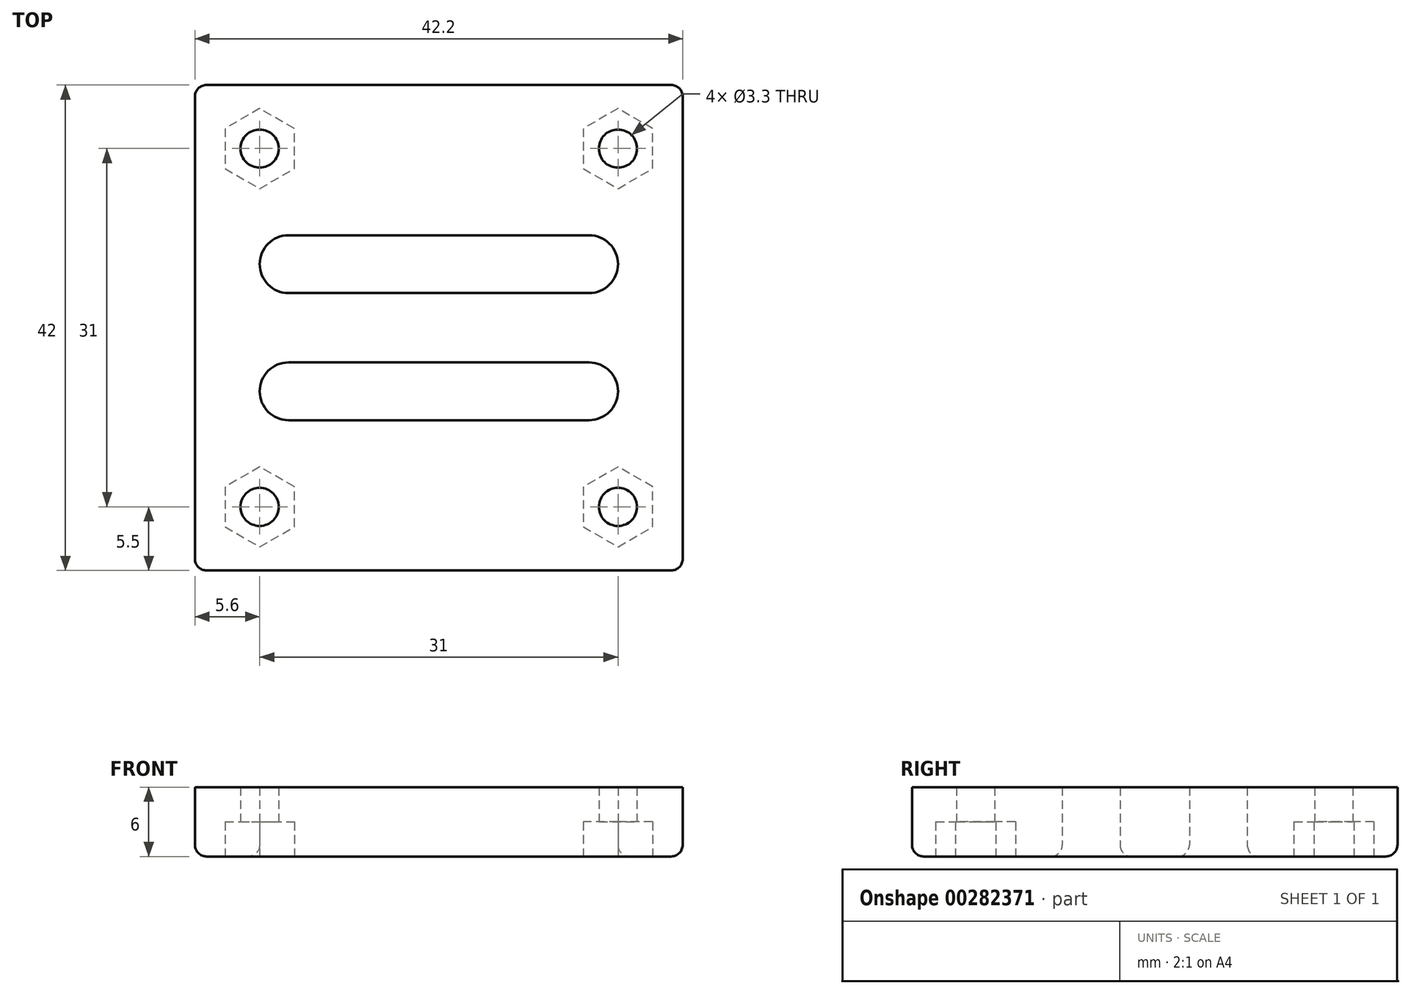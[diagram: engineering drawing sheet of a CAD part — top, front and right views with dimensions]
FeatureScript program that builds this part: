
annotation { "Feature Type Name" : "Feature", "Feature Type Description" : "" }
export const myFeature = defineFeature(function(context is Context, id is Id, definition is map)
    precondition{}
    {
        {
            var Q0;
            Q0=qCreatedBy(makeId("Top.planeOp"),FACE);
            var sketch = newSketch(context, id + "F0", { "sketchPlane" : qUnion([Q0])});
            skLineSegment(sketch, "E0.bottom", {"start": v(21.1, 21) * mm, "end": v(-21.1, 21) * mm});
            skLineSegment(sketch, "E0.top", {"start": v(21.1, -21) * mm, "end": v(-21.1, -21) * mm});
            skLineSegment(sketch, "E0.left", {"start": v(21.1, 21) * mm, "end": v(21.1, -21) * mm});
            skLineSegment(sketch, "E0.right", {"start": v(-21.1, 21) * mm, "end": v(-21.1, -21) * mm});
            skPoint(sketch, "E0.middle", {"position": v(0, 0) * mm});
            skLineSegment(sketch, "E1.bottom", {"start": v(15.5, 15.5) * mm, "end": v(-15.5, 15.5) * mm, "construction": true});
            skLineSegment(sketch, "E1.top", {"start": v(15.5, -15.5) * mm, "end": v(-15.5, -15.5) * mm, "construction": true});
            skLineSegment(sketch, "E1.left", {"start": v(15.5, 15.5) * mm, "end": v(15.5, -15.5) * mm, "construction": true});
            skLineSegment(sketch, "E1.right", {"start": v(-15.5, 15.5) * mm, "end": v(-15.5, -15.5) * mm, "construction": true});
            skLineSegment(sketch, "E2", {"start": v(0, -15.5) * mm, "end": v(0, 15.5) * mm, "construction": true});
            skLineSegment(sketch, "E3", {"start": v(-13, 5.5) * mm, "end": v(13, 5.5) * mm, "construction": true});
            skLineSegment(sketch, "E4", {"start": v(-13, -5.5) * mm, "end": v(13, -5.5) * mm, "construction": true});
            skArc(sketch, "E5.0.startCap", {"start": v(-13, -8) * mm, "mid": v(-15.5, -5.5) * mm, "end": v(-13, -3) * mm});
            skArc(sketch, "E5.0.endCap", {"start": v(13, -3) * mm, "mid": v(15.5, -5.5) * mm, "end": v(13, -8) * mm});
            skLineSegment(sketch, "E5.0.left", {"start": v(-13, -3) * mm, "end": v(13, -3) * mm});
            skLineSegment(sketch, "E5.0.right", {"start": v(-13, -8) * mm, "end": v(13, -8) * mm});
            skArc(sketch, "E6.0.startCap", {"start": v(-13, 3) * mm, "mid": v(-15.5, 5.5) * mm, "end": v(-13, 8) * mm});
            skArc(sketch, "E6.0.endCap", {"start": v(13, 8) * mm, "mid": v(15.5, 5.5) * mm, "end": v(13, 3) * mm});
            skLineSegment(sketch, "E6.0.left", {"start": v(-13, 8) * mm, "end": v(13, 8) * mm});
            skLineSegment(sketch, "E6.0.right", {"start": v(-13, 3) * mm, "end": v(13, 3) * mm});
            skSolve(sketch);
        }
        {
            var Q0;
            Q0=qSketchRegion(id+"F0",true);
            extrude(context, id + "F1", {"entities" : qUnion([Q0]), "depth" : 6 * mm});
        }
        {
            var Q0;
            Q0=makeQuery(id+"F1.opExtrude","CAP_FACE",FACE,{"disambiguationData":[OSD([sQuery(id+"F0.wireOp",EDGE,"E0.bottom"),sQuery(id+"F0.wireOp",EDGE,"E0.top"),sQuery(id+"F0.wireOp",EDGE,"E0.left"),sQuery(id+"F0.wireOp",EDGE,"E0.right"),sQuery(id+"F0.wireOp",EDGE,"E5.0.startCap"),sQuery(id+"F0.wireOp",EDGE,"E5.0.endCap"),sQuery(id+"F0.wireOp",EDGE,"E5.0.left"),sQuery(id+"F0.wireOp",EDGE,"E5.0.right"),sQuery(id+"F0.wireOp",EDGE,"E6.0.startCap"),sQuery(id+"F0.wireOp",EDGE,"E6.0.endCap"),sQuery(id+"F0.wireOp",EDGE,"E6.0.left"),sQuery(id+"F0.wireOp",EDGE,"E6.0.right")])],"isStart":true});
            var sketch = newSketch(context, id + "F2", { "sketchPlane" : qUnion([Q0])});
            skLineSegment(sketch, "E7.bottom", {"start": v(15.5, 15.5) * mm, "end": v(-15.5, 15.5) * mm, "construction": true});
            skLineSegment(sketch, "E7.top", {"start": v(15.5, -15.5) * mm, "end": v(-15.5, -15.5) * mm, "construction": true});
            skLineSegment(sketch, "E7.left", {"start": v(15.5, 15.5) * mm, "end": v(15.5, -15.5) * mm, "construction": true});
            skLineSegment(sketch, "E7.right", {"start": v(-15.5, 15.5) * mm, "end": v(-15.5, -15.5) * mm, "construction": true});
            skPoint(sketch, "E7.middle", {"position": v(0, 0) * mm});
            skPoint(sketch, "E8", {"position": v(-15.5, 15.5) * mm});
            skPoint(sketch, "E9", {"position": v(15.5, 15.5) * mm});
            skPoint(sketch, "E10", {"position": v(15.5, -15.5) * mm});
            skPoint(sketch, "E11", {"position": v(-15.5, -15.5) * mm});
            skCircle(sketch, "E12.cCircle", {"center": v(-15.5, 15.5) * mm, "radius": 3 * mm, "construction": true});
            skLineSegment(sketch, "E12.0", {"start": v(-12.5, 17.23) * mm, "end": v(-12.5, 13.77) * mm});
            skLineSegment(sketch, "E12.1", {"start": v(-12.5, 13.77) * mm, "end": v(-15.5, 12.04) * mm});
            skLineSegment(sketch, "E12.2", {"start": v(-15.5, 12.04) * mm, "end": v(-18.5, 13.77) * mm});
            skLineSegment(sketch, "E12.3", {"start": v(-18.5, 13.77) * mm, "end": v(-18.5, 17.23) * mm});
            skLineSegment(sketch, "E12.4", {"start": v(-18.5, 17.23) * mm, "end": v(-15.5, 18.96) * mm});
            skLineSegment(sketch, "E12.5", {"start": v(-15.5, 18.96) * mm, "end": v(-12.5, 17.23) * mm});
            skPoint(sketch, "E12.0.midPoint", {"position": v(-12.5, 15.5) * mm});
            skCircle(sketch, "E13.cCircle", {"center": v(15.5, 15.5) * mm, "radius": 3 * mm, "construction": true});
            skLineSegment(sketch, "E13.0", {"start": v(12.5, 13.77) * mm, "end": v(12.5, 17.23) * mm});
            skLineSegment(sketch, "E13.1", {"start": v(12.5, 17.23) * mm, "end": v(15.5, 18.96) * mm});
            skLineSegment(sketch, "E13.2", {"start": v(15.5, 18.96) * mm, "end": v(18.5, 17.23) * mm});
            skLineSegment(sketch, "E13.3", {"start": v(18.5, 17.23) * mm, "end": v(18.5, 13.77) * mm});
            skLineSegment(sketch, "E13.4", {"start": v(18.5, 13.77) * mm, "end": v(15.5, 12.04) * mm});
            skLineSegment(sketch, "E13.5", {"start": v(15.5, 12.04) * mm, "end": v(12.5, 13.77) * mm});
            skPoint(sketch, "E13.0.midPoint", {"position": v(12.5, 15.5) * mm});
            skCircle(sketch, "E14.cCircle", {"center": v(15.5, -15.5) * mm, "radius": 3 * mm, "construction": true});
            skLineSegment(sketch, "E14.0", {"start": v(12.5, -17.23) * mm, "end": v(12.5, -13.77) * mm});
            skLineSegment(sketch, "E14.1", {"start": v(12.5, -13.77) * mm, "end": v(15.5, -12.04) * mm});
            skLineSegment(sketch, "E14.2", {"start": v(15.5, -12.04) * mm, "end": v(18.5, -13.77) * mm});
            skLineSegment(sketch, "E14.3", {"start": v(18.5, -13.77) * mm, "end": v(18.5, -17.23) * mm});
            skLineSegment(sketch, "E14.4", {"start": v(18.5, -17.23) * mm, "end": v(15.5, -18.96) * mm});
            skLineSegment(sketch, "E14.5", {"start": v(15.5, -18.96) * mm, "end": v(12.5, -17.23) * mm});
            skPoint(sketch, "E14.0.midPoint", {"position": v(12.5, -15.5) * mm});
            skCircle(sketch, "E15.cCircle", {"center": v(-15.5, -15.5) * mm, "radius": 3 * mm, "construction": true});
            skLineSegment(sketch, "E15.0", {"start": v(-12.5, -13.77) * mm, "end": v(-12.5, -17.23) * mm});
            skLineSegment(sketch, "E15.1", {"start": v(-12.5, -17.23) * mm, "end": v(-15.5, -18.96) * mm});
            skLineSegment(sketch, "E15.2", {"start": v(-15.5, -18.96) * mm, "end": v(-18.5, -17.23) * mm});
            skLineSegment(sketch, "E15.3", {"start": v(-18.5, -17.23) * mm, "end": v(-18.5, -13.77) * mm});
            skLineSegment(sketch, "E15.4", {"start": v(-18.5, -13.77) * mm, "end": v(-15.5, -12.04) * mm});
            skLineSegment(sketch, "E15.5", {"start": v(-15.5, -12.04) * mm, "end": v(-12.5, -13.77) * mm});
            skPoint(sketch, "E15.0.midPoint", {"position": v(-12.5, -15.5) * mm});
            skSolve(sketch);
        }
        {
            var Q0;
            Q0=makeQuery(id+"F1.opExtrude","SWEPT_EDGE",EDGE,{"disambiguationData":[OSD([sQuery(id+"F0.wireOp",EDGE,"E0.top"),sQuery(id+"F0.wireOp",EDGE,"E0.right")])]});
            var Q1;
            Q1=makeQuery(id+"F1.opExtrude","SWEPT_EDGE",EDGE,{"disambiguationData":[OSD([sQuery(id+"F0.wireOp",EDGE,"E0.top"),sQuery(id+"F0.wireOp",EDGE,"E0.left")])]});
            var Q2;
            Q2=makeQuery(id+"F1.opExtrude","SWEPT_EDGE",EDGE,{"disambiguationData":[OSD([sQuery(id+"F0.wireOp",EDGE,"E0.bottom"),sQuery(id+"F0.wireOp",EDGE,"E0.right")])]});
            var Q3;
            Q3=makeQuery(id+"F1.opExtrude","SWEPT_EDGE",EDGE,{"disambiguationData":[OSD([sQuery(id+"F0.wireOp",EDGE,"E0.bottom"),sQuery(id+"F0.wireOp",EDGE,"E0.left")])]});
            fillet(context, id + "F3", {"entities" : qUnion([Q0, Q1, Q2, Q3]), "radius" : 1 * mm, "tangentPropagation" : true, "allowEdgeOverflow" : false});
        }
        {
            var Q0;
            Q0=makeQuery(id+"F1.opExtrude","CAP_EDGE",EDGE,{"disambiguationData":[OSD([sQuery(id+"F0.wireOp",EDGE,"E0.top")])],"isStart":true});
            var Q1;
            Q1=makeQuery(id+"F1.opExtrude","CAP_EDGE",EDGE,{"disambiguationData":[OSD([sQuery(id+"F0.wireOp",EDGE,"E5.0.left")])],"isStart":true});
            var Q2;
            Q2=makeQuery(id+"F1.opExtrude","CAP_EDGE",EDGE,{"disambiguationData":[OSD([sQuery(id+"F0.wireOp",EDGE,"E6.0.left")])],"isStart":true});
            fillet(context, id + "F4", {"entities" : qUnion([Q0, Q1, Q2]), "radius" : 1 * mm, "tangentPropagation" : true, "allowEdgeOverflow" : false});
        }
        {
            var Q0;
            Q0 = qSketchRegion(id + "F2", true);
            extrude(context, id + "F5", {"entities" : qUnion([Q0]), "operationType" : NewBodyOperationType.REMOVE, "oppositeDirection" : true, "depth" : 3 * mm});
        }
        {
            var Q0;
            Q0=makeQuery(id+"F1.opExtrude","CAP_FACE",FACE,{"disambiguationData":[OSD([sQuery(id+"F0.wireOp",EDGE,"E0.bottom"),sQuery(id+"F0.wireOp",EDGE,"E0.top"),sQuery(id+"F0.wireOp",EDGE,"E0.left"),sQuery(id+"F0.wireOp",EDGE,"E0.right"),sQuery(id+"F0.wireOp",EDGE,"E5.0.startCap"),sQuery(id+"F0.wireOp",EDGE,"E5.0.endCap"),sQuery(id+"F0.wireOp",EDGE,"E5.0.left"),sQuery(id+"F0.wireOp",EDGE,"E5.0.right"),sQuery(id+"F0.wireOp",EDGE,"E6.0.startCap"),sQuery(id+"F0.wireOp",EDGE,"E6.0.endCap"),sQuery(id+"F0.wireOp",EDGE,"E6.0.left"),sQuery(id+"F0.wireOp",EDGE,"E6.0.right")])],"isStart":true});
            var sketch = newSketch(context, id + "F6", { "sketchPlane" : qUnion([Q0])});
            skLineSegment(sketch, "E16", {"start": v(-15.5, 18.96) * mm, "end": v(-15.5, 12.04) * mm, "construction": true});
            skLineSegment(sketch, "E17", {"start": v(15.5, 18.96) * mm, "end": v(15.5, 12.04) * mm, "construction": true});
            skLineSegment(sketch, "E18", {"start": v(-15.5, -12.04) * mm, "end": v(-15.5, -18.96) * mm, "construction": true});
            skLineSegment(sketch, "E19", {"start": v(15.5, -12.04) * mm, "end": v(15.5, -18.96) * mm, "construction": true});
            skCircle(sketch, "E20", {"center": v(-15.5, 15.5) * mm, "radius": 1.65 * mm});
            skCircle(sketch, "E21", {"center": v(15.5, 15.5) * mm, "radius": 1.65 * mm});
            skCircle(sketch, "E22", {"center": v(15.5, -15.5) * mm, "radius": 1.65 * mm});
            skCircle(sketch, "E23", {"center": v(-15.5, -15.5) * mm, "radius": 1.65 * mm});
            skSolve(sketch);
        }
        {
            var Q0;
            Q0 = qSketchRegion(id + "F6", true);
            extrude(context, id + "F7", {"entities" : qUnion([Q0]), "operationType" : NewBodyOperationType.REMOVE, "endBound" : BoundingType.THROUGH_ALL, "oppositeDirection" : true, "depth" : 25 * mm});
        }
    });
